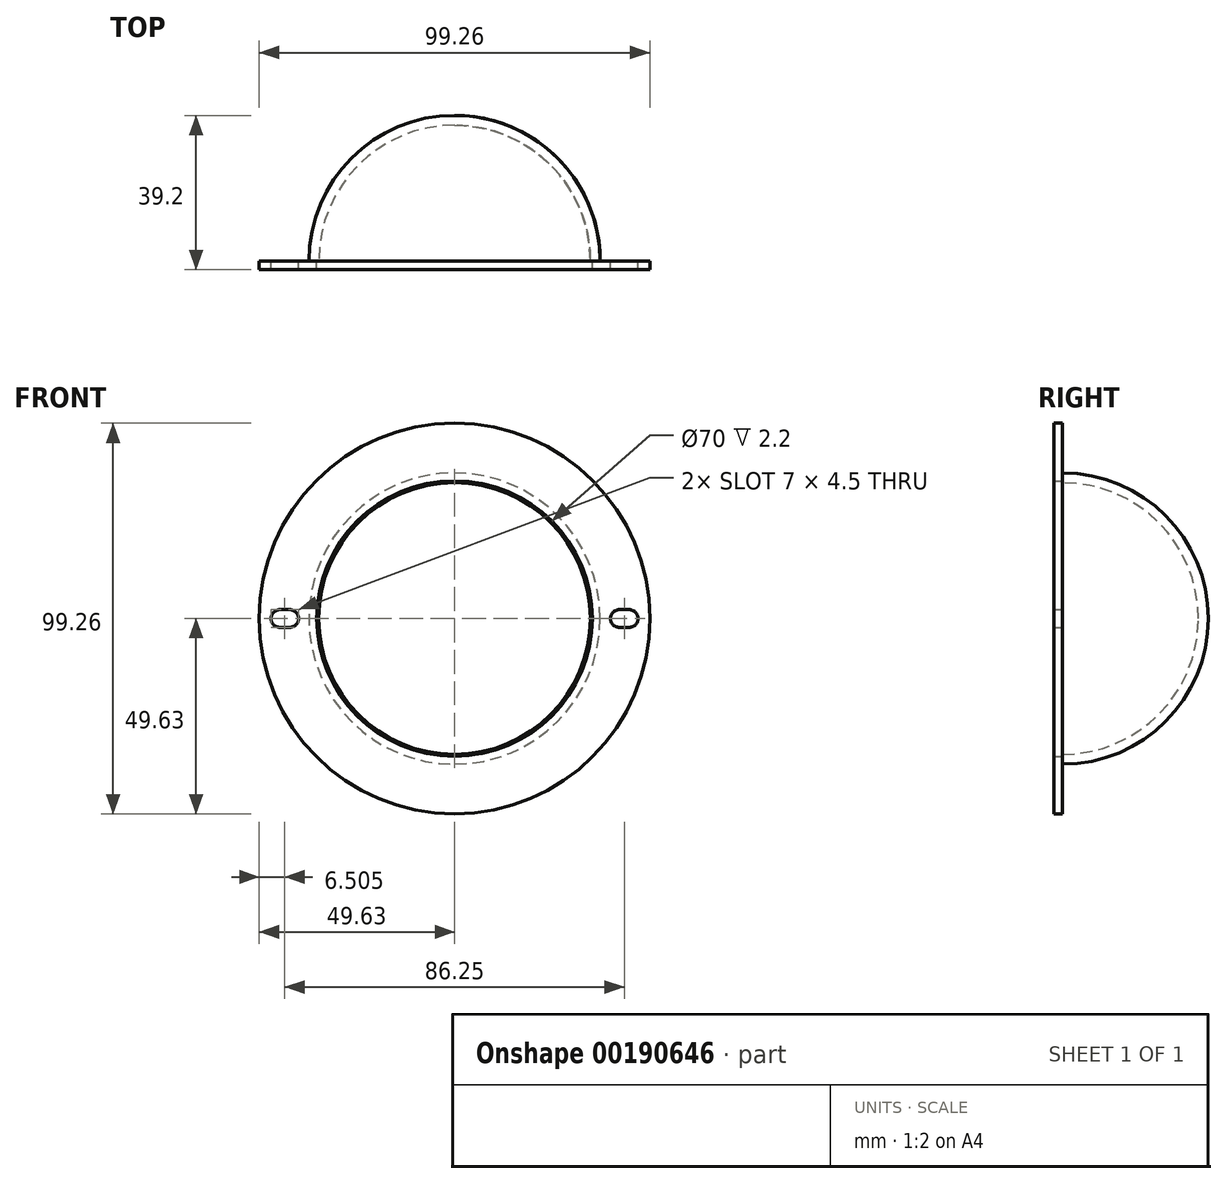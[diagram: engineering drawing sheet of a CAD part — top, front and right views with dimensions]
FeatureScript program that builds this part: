
annotation { "Feature Type Name" : "Feature", "Feature Type Description" : "" }
export const myFeature = defineFeature(function(context is Context, id is Id, definition is map)
    precondition{}
    {
        {
            var Q0;
            Q0=qCreatedBy(makeId("Front.planeOp"),FACE);
            var sketch = newSketch(context, id + "F0", { "sketchPlane" : qUnion([Q0])});
            skArc(sketch, "E0", {"start": v(-44.38, 2.25) * mm, "mid": v(-46.63, 0) * mm, "end": v(-44.38, -2.25) * mm});
            skArc(sketch, "E1", {"start": v(-41.88, -2.25) * mm, "mid": v(-39.62, 0) * mm, "end": v(-41.88, 2.25) * mm});
            skLineSegment(sketch, "E2", {"start": v(-44.38, 2.25) * mm, "end": v(-41.88, 2.25) * mm});
            skLineSegment(sketch, "E3", {"start": v(-44.38, -2.25) * mm, "end": v(-41.88, -2.25) * mm});
            skCircle(sketch, "E4", {"center": v(0, 0) * mm, "radius": 35 * mm});
            skArc(sketch, "E5.MirrorCS", {"start": v(41.88, -2.25) * mm, "mid": v(39.62, 0) * mm, "end": v(41.88, 2.25) * mm});
            skLineSegment(sketch, "E6.MirrorCS", {"start": v(44.38, 2.25) * mm, "end": v(41.88, 2.25) * mm});
            skArc(sketch, "E7.MirrorCS", {"start": v(44.38, 2.25) * mm, "mid": v(46.63, 0) * mm, "end": v(44.38, -2.25) * mm});
            skLineSegment(sketch, "E8.MirrorCS", {"start": v(44.38, -2.25) * mm, "end": v(41.88, -2.25) * mm});
            skCircle(sketch, "E9", {"center": v(0, 0) * mm, "radius": 49.62 * mm});
            skSolve(sketch);
        }
        {
            var Q0;
            Q0=makeQuery(id+"F0.imprint","IMPRINT",FACE,{"disambiguationData":[TD([[makeQuery(id+"F0.imprint","IMPRINT",EDGE,{"derivedFrom":sQuery(id+"F0.wireOp",EDGE,"E0")}),-1.0]])]});
            extrude(context, id + "F1", {"entities" : qUnion([Q0]), "depth" : 2.2 * mm});
        }
        {
            var Q0;
            Q0=qCreatedBy(makeId("Top.planeOp"),FACE);
            var sketch = newSketch(context, id + "F2", { "sketchPlane" : qUnion([Q0])});
            skArc(sketch, "E10", {"start": v(37, 0) * mm, "mid": v(26.16, 26.16) * mm, "end": v(0, 37) * mm});
            skLineSegment(sketch, "E11", {"start": v(0, 0) * mm, "end": v(0, 37) * mm});
            skLineSegment(sketch, "E12", {"start": v(0, 0) * mm, "end": v(0, 0) * mm});
            skLineSegment(sketch, "E13", {"start": v(0, 0) * mm, "end": v(37, 0) * mm});
            skSolve(sketch);
        }
        {
            var Q0;
            Q0=makeQuery(id+"F2.imprint","IMPRINT",FACE,{"disambiguationData":[TD([[makeQuery(id+"F2.imprint","IMPRINT",EDGE,{"derivedFrom":sQuery(id+"F2.wireOp",EDGE,"XMLjtoeJ-EviQ-A96v-KwvO-TNBCJdwhLSXw")}),1.0]])]});
            var Q1;
            Q1=makeQuery(id+"F2.imprint","IMPRINT",FACE,{"disambiguationData":[TD([[makeQuery(id+"F2.imprint","IMPRINT",EDGE,{"derivedFrom":sQuery(id+"F2.wireOp",EDGE,"E10")}),1.0]])]});
            var Q2;
            Q2=sQuery(id+"F2.wireOp",EDGE,"E11");
            revolve(context, id + "F3", {"operationType" : NewBodyOperationType.ADD, "entities" : qUnion([Q0, Q1]), "axis" : qUnion([Q2]), "revolveType" : RevolveType.FULL});
        }
        {
            var Q0;
            Q0=makeQuery(id+"F3.opRevolve","SWEPT_FACE",FACE,{"disambiguationData":[OSD([sQuery(id+"F2.wireOp",EDGE,"E13")])]});
            shell(context, id + "F4", {"entities" : qUnion([Q0]), "thickness" : 2.5 * mm});
        }
    });
